# Revit family: Storage-Teknion-LWBOH-Byward_Open_High_Tower-R2022
name_source: partatom
category: Furniture
units: mm (PartAtom-declared; Revit-internal decimal feet)

## family parameters
Always vertical = Yes
Cut with Voids When Loaded = No
OmniClass Number = 23.40.20.00
OmniClass Title = General Furniture and Specialties
Render Appearance Source = Family Geometry
Room Calculation Point = No
Shared = Yes
Work Plane-Based = No

## types (2) — shared parameters
Assembly Code = E2020200
Height = 60 "
Manufacturer = Teknion
Manufacturer Fax = 416.661.4586
Part Number = LWBOH
Product Documentation Link = https://assets.teknion.com
Product Line = Byward
Product Page URL = https://www.teknion.com
Series = Byward
Sustainability Data = https://www.teknion.com
URL = www.teknion.com
Unit Weight URL = http://www.teknion.com
Warranty = http://www.teknion.com
zero-valued in all types: Default Elevation

## per-type parameters (varying)
| type | Case Finish | Description | Left Casual Drawer | Model | Right Casual Drawer |
| Left Open, Right Coat | Veneer-Teknion-5U-Flintwood-Raw_Umber (Long Grain) | Byward Open High Tower, Lite Wood Office, Left Open, Right Coat | No | LWBOH_____ | Yes |
| Left Coat, Right Open | Source Laminate - Teknion - XS - Storm White | Byward Open High Tower, Lite Wood Office, Left Coat, Right Open | Yes | LWBOHJO60_____ | No |

## geometry (parser evidence)
native form markers: Sweep x9
no freeform markers — native parametric forms only
